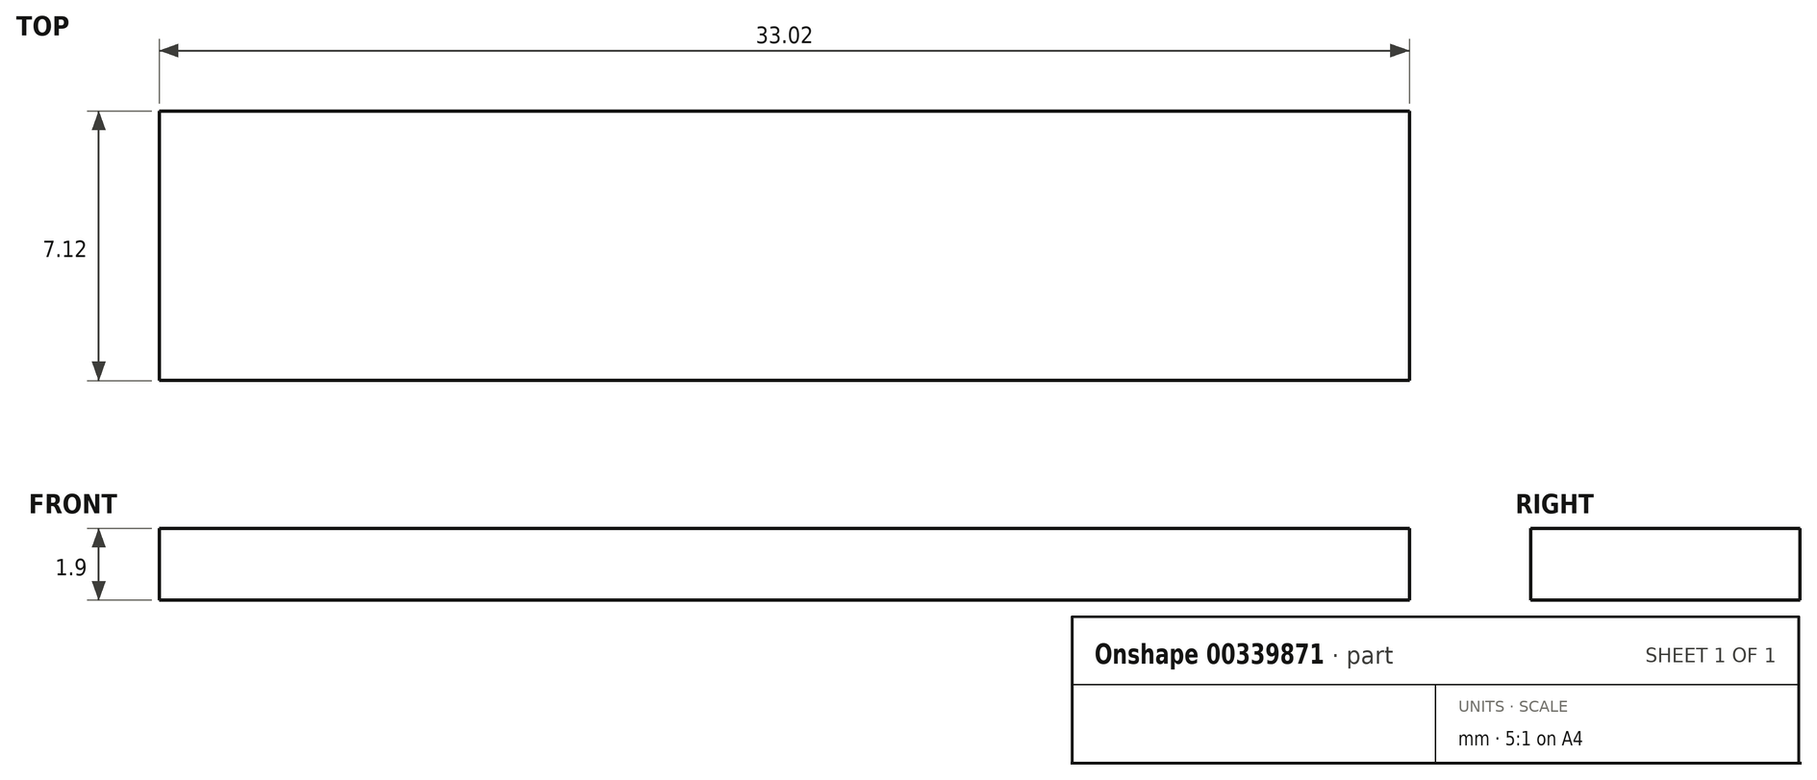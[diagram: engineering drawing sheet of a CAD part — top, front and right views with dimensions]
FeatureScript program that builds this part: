
annotation { "Feature Type Name" : "Feature", "Feature Type Description" : "" }
export const myFeature = defineFeature(function(context is Context, id is Id, definition is map)
    precondition{}
    {
        {
            var Q0;
            Q0=qCreatedBy(makeId("Top.planeOp"),FACE);
            var sketch = newSketch(context, id + "F0", { "sketchPlane" : qUnion([Q0])});
            skLineSegment(sketch, "E0.bottom", {"start": v(-16.65, 17.19) * mm, "end": v(16.37, 17.19) * mm});
            skLineSegment(sketch, "E0.top", {"start": v(-16.65, 10.07) * mm, "end": v(16.37, 10.07) * mm});
            skLineSegment(sketch, "E0.left", {"start": v(-16.65, 17.19) * mm, "end": v(-16.65, 10.07) * mm});
            skLineSegment(sketch, "E0.right", {"start": v(16.37, 17.19) * mm, "end": v(16.37, 10.07) * mm});
            skSolve(sketch);
        }
        {
            var Q0;
            Q0=makeQuery(id+"F0.imprint","IMPRINT",FACE,{"disambiguationData":[TD([[makeQuery(id+"F0.imprint","IMPRINT",EDGE,{"derivedFrom":sQuery(id+"F0.wireOp",EDGE,"E0.bottom")}),-1.0]])]});
            extrude(context, id + "F1", {"entities" : qUnion([Q0]), "depth" : 1.9 * mm});
        }
    });
